# Revit family: KEUCO_14967010001
name_source: partatom
category: Allgemeines Modell
revit_build: Autodesk Revit 2016 (Build: 20150220_1215(x64)
units: mm (PartAtom-declared; Revit-internal decimal feet)

## family parameters
Arbeitsebenenbasiert = Ja
Beim Laden mit Abzugskörper schneiden = Nein
Bemaßung runder Anschluss = Durchmesser verwenden
Gemeinsam genutzt = Nein
Immer vertikal = Nein
Kann Basisbauteil für Bewehrung sein = Nein
Raumberechnungspunkt = Nein
Teiletyp = Normal

## types (3) — shared parameters
Beschreibung = mit Deckel und Gehäuse aus Metall,
mit herausnehmbarer Kunststoff-Innenbox (lichtgrau),
für maximale Packungsgröße 145 x 102 x 43 mm
Gewicht = 2.718
Hersteller = KEUCO
Kategorie = ACC
Rail Length = 851 mm
Serie = Plan
URL = https://www.keuco.com
Verwendung = WC
Vorgabe-Ansicht = 1219 mm

## per-type parameters (varying)
| type | Ausschreibungstext | Stange Material |
| 14967070001 | KEUCO PLAN Feuchtpapierbox, 14967070001
Deckel und Gehäuse aus Metall in Edelstahl-Optik,
herausnehmbare Kunststoff-Innenbox in lichtgrau (RAL 7035),
in ästhetischem, funktionalem Design, Ecken gerundet,
Wandmodell, leicht zu reinigen,
Höhe 58 mm, Breite 165 mm, Ausladung 139 mm,
für maximale Packungsgröße 145 mm x 102 mm x 43 mm,
die Feuchtpapierbox wird verdeckt angebracht,
Lieferung inkl. korrosionsfreiem Befestigungsmaterial | Edelstahl |
| 14967170001 | KEUCO PLAN Feuchtpapierbox, 14967170001
hochglanzverchromtes Deckel und 
Gehäuse aus silber-eloxiertem Alumiun (E6 EV1),
herausnehmbare Kunststoff-Innenbox in lichtgrau (RAL 7035),
in ästhetischem, funktionalem Design, Ecken gerundet,
Wandmodell, leicht zu reinigen,
Höhe 58 mm, Breite 165 mm, Ausladung 139 mm,
für maximale Packungsgröße 145 mm x 102 mm x 43 mm,
die Feuchtpapierbox wird verdeckt angebracht,
Lieferung inkl. korrosionsfreiem Befestigungsmaterial | Edelstahl |
| 14967010001 | KEUCO PLAN Feuchtpapierbox, 14967010001
mit hochglanzverchromtem Deckel und Gehäuse aus Metall,
herausnehmbare Kunststoff-Innenbox in lichtgrau (RAL 7035),
in ästhetischem, funktionalem Design, Ecken gerundet,
Wandmodell, leicht zu reinigen,
Höhe 58 mm, Breite 165 mm, Ausladung 139 mm,
für maximale Packungsgröße 145 mm x 102 mm x 43 mm,
die Feuchtpapierbox wird verdeckt angebracht,
Lieferung inkl. korrosionsfreiem Befestigungsmaterial | Verchromt |

note: column(s) folded — value = type name in every type: Artikelnummer

## geometry (parser evidence)
native form markers: Blend x9, Sweep x3
no freeform markers — native parametric forms only
